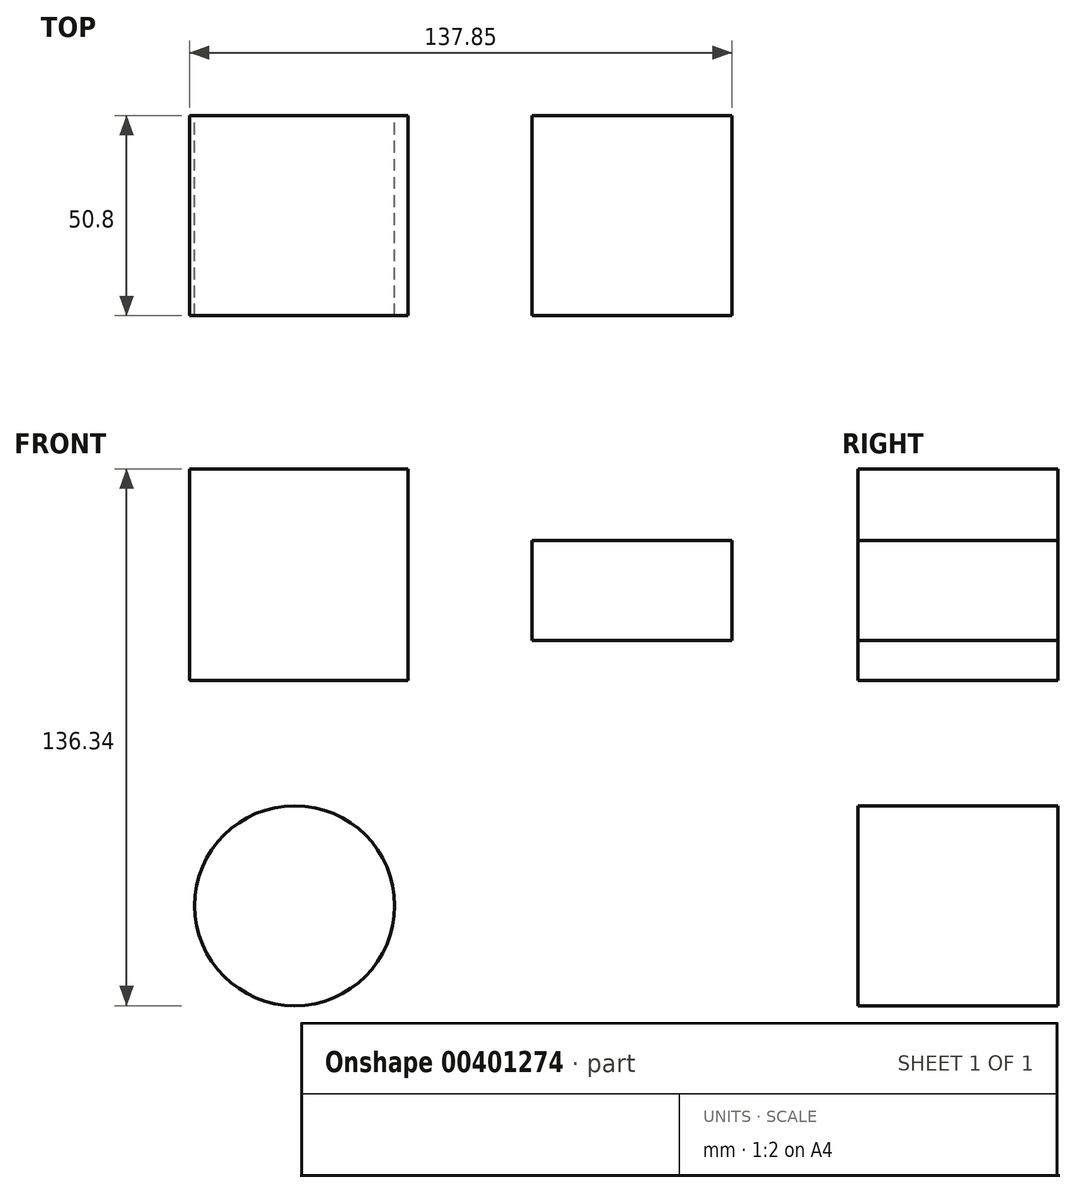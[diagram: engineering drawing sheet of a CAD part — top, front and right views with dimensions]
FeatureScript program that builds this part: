
annotation { "Feature Type Name" : "Feature", "Feature Type Description" : "" }
export const myFeature = defineFeature(function(context is Context, id is Id, definition is map)
    precondition{}
    {
        {
            var Q0;
            Q0=qCreatedBy(makeId("Front.planeOp"),FACE);
            var sketch = newSketch(context, id + "F0", { "sketchPlane" : qUnion([Q0])});
            skLineSegment(sketch, "E0.bottom", {"start": v(-70.24, 65.82) * mm, "end": v(-14.65, 65.82) * mm});
            skLineSegment(sketch, "E0.top", {"start": v(-70.24, 12.1) * mm, "end": v(-14.65, 12.1) * mm});
            skLineSegment(sketch, "E0.left", {"start": v(-70.24, 65.82) * mm, "end": v(-70.24, 12.1) * mm});
            skLineSegment(sketch, "E0.right", {"start": v(-14.65, 65.82) * mm, "end": v(-14.65, 12.1) * mm});
            skLineSegment(sketch, "E1.bottom", {"start": v(-41.87, 20.7) * mm, "end": v(-41.87, 20.7) * mm});
            skSolve(sketch);
        }
        {
            var Q0;
            Q0=qCreatedBy(makeId("Front.planeOp"),FACE);
            var sketch = newSketch(context, id + "F1", { "sketchPlane" : qUnion([Q0])});
            skLineSegment(sketch, "E2.bottom", {"start": v(16.81, 22.23) * mm, "end": v(67.61, 22.23) * mm});
            skLineSegment(sketch, "E2.top", {"start": v(16.81, 47.63) * mm, "end": v(67.61, 47.63) * mm});
            skLineSegment(sketch, "E2.left", {"start": v(16.81, 22.23) * mm, "end": v(16.81, 47.63) * mm});
            skLineSegment(sketch, "E2.right", {"start": v(67.61, 22.23) * mm, "end": v(67.61, 47.63) * mm});
            skSolve(sketch);
        }
        {
            var Q0;
            Q0=qCreatedBy(makeId("Front.planeOp"),FACE);
            var sketch = newSketch(context, id + "F2", { "sketchPlane" : qUnion([Q0])});
            skCircle(sketch, "E3", {"center": v(-43.5, -45.12) * mm, "radius": 25.4 * mm});
            skSolve(sketch);
        }
        {
            var Q0;
            Q0=makeQuery(id+"F0.imprint","IMPRINT",FACE,{"disambiguationData":[TD([[makeQuery(id+"F0.imprint","IMPRINT",EDGE,{"derivedFrom":sQuery(id+"F0.wireOp",EDGE,"E0.bottom")}),-1.0]])]});
            extrude(context, id + "F3", {"entities" : qUnion([Q0]), "depth" : 50.8 * mm});
        }
        {
            var Q0;
            Q0 = qSketchRegion(id + "F1", true);
            extrude(context, id + "F4", {"entities" : qUnion([Q0]), "depth" : 50.8 * mm});
        }
        {
            var Q0;
            Q0=makeQuery(id+"F2.imprint","IMPRINT",FACE,{"disambiguationData":[TD([[makeQuery(id+"F2.imprint","IMPRINT",EDGE,{"derivedFrom":sQuery(id+"F2.wireOp",EDGE,"E3")}),1.0]])]});
            extrude(context, id + "F5", {"entities" : qUnion([Q0]), "depth" : 50.8 * mm});
        }
    });
